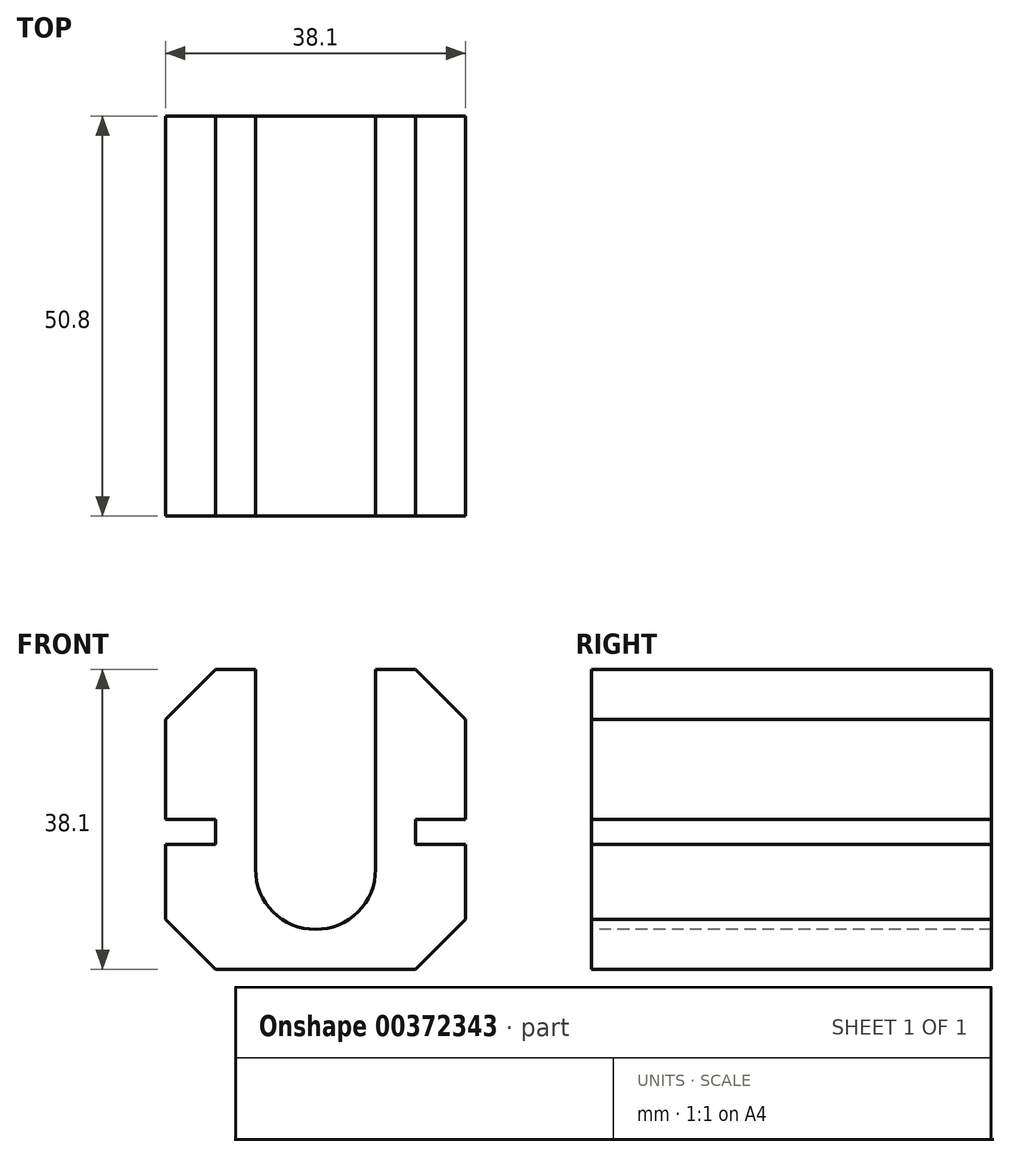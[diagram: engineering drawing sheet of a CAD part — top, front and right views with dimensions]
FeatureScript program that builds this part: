
annotation { "Feature Type Name" : "Feature", "Feature Type Description" : "" }
export const myFeature = defineFeature(function(context is Context, id is Id, definition is map)
    precondition{}
    {
        {
            var Q0;
            Q0=qCreatedBy(makeId("Front.planeOp"),FACE);
            var sketch = newSketch(context, id + "F0", { "sketchPlane" : qUnion([Q0])});
            skLineSegment(sketch, "E0", {"start": v(-12.7, 19.05) * mm, "end": v(-19.05, 12.7) * mm});
            skLineSegment(sketch, "E1", {"start": v(12.7, 19.05) * mm, "end": v(19.05, 12.7) * mm});
            skLineSegment(sketch, "E2", {"start": v(-12.7, -19.05) * mm, "end": v(-19.05, -12.7) * mm});
            skLineSegment(sketch, "E3", {"start": v(12.7, -19.05) * mm, "end": v(19.05, -12.7) * mm});
            skLineSegment(sketch, "E4", {"start": v(-12.7, 19.05) * mm, "end": v(12.7, 19.05) * mm});
            skLineSegment(sketch, "E5", {"start": v(-19.05, 12.7) * mm, "end": v(-19.05, -12.7) * mm});
            skLineSegment(sketch, "E6", {"start": v(19.05, 12.7) * mm, "end": v(19.05, -12.7) * mm});
            skLineSegment(sketch, "E7", {"start": v(-12.7, -19.05) * mm, "end": v(12.7, -19.05) * mm});
            skSolve(sketch);
        }
        {
            var Q0;
            Q0=qCreatedBy(makeId("Front.planeOp"),FACE);
            var sketch = newSketch(context, id + "F1", { "sketchPlane" : qUnion([Q0])});
            skLineSegment(sketch, "E8.bottom", {"start": v(-19.05, 0) * mm, "end": v(-12.7, 0) * mm});
            skLineSegment(sketch, "E8.top", {"start": v(-19.05, -3.18) * mm, "end": v(-12.7, -3.18) * mm});
            skLineSegment(sketch, "E8.left", {"start": v(-19.05, 0) * mm, "end": v(-19.05, -3.18) * mm});
            skLineSegment(sketch, "E8.right", {"start": v(-12.7, 0) * mm, "end": v(-12.7, -3.18) * mm});
            skSolve(sketch);
        }
        {
            var Q0;
            Q0=qCreatedBy(makeId("Front.planeOp"),FACE);
            var sketch = newSketch(context, id + "F2", { "sketchPlane" : qUnion([Q0])});
            skLineSegment(sketch, "E9.bottom", {"start": v(12.7, 0) * mm, "end": v(19.05, 0) * mm});
            skLineSegment(sketch, "E9.top", {"start": v(12.7, -3.17) * mm, "end": v(19.05, -3.17) * mm});
            skLineSegment(sketch, "E9.left", {"start": v(12.7, 0) * mm, "end": v(12.7, -3.17) * mm});
            skLineSegment(sketch, "E9.right", {"start": v(19.05, 0) * mm, "end": v(19.05, -3.17) * mm});
            skSolve(sketch);
        }
        {
            var Q0;
            Q0=qSketchRegion(id+"F0",true);
            extrude(context, id + "F3", {"entities" : qUnion([Q0]), "endBound" : BoundingType.SYMMETRIC, "depth" : 50.8 * mm});
        }
        {
            var Q0;
            Q0 = qSketchRegion(id + "F2", true);
            var Q1;
            Q1 = qSketchRegion(id + "F1", true);
            extrude(context, id + "F4", {"entities" : qUnion([Q0, Q1]), "operationType" : NewBodyOperationType.REMOVE, "endBound" : BoundingType.SYMMETRIC, "oppositeDirection" : true, "depth" : 50.8 * mm});
        }
        {
            var Q0;
            Q0=qCreatedBy(makeId("Front.planeOp"),FACE);
            var sketch = newSketch(context, id + "F5", { "sketchPlane" : qUnion([Q0])});
            skLineSegment(sketch, "E10.bottom", {"start": v(-7.62, 19.05) * mm, "end": v(7.62, 19.05) * mm});
            skLineSegment(sketch, "E10.left", {"start": v(-7.62, 19.05) * mm, "end": v(-7.62, -6.35) * mm});
            skLineSegment(sketch, "E10.right", {"start": v(7.62, 19.05) * mm, "end": v(7.62, -6.35) * mm});
            skArc(sketch, "E11", {"start": v(-7.62, -6.35) * mm, "mid": v(0, -13.97) * mm, "end": v(7.62, -6.35) * mm});
            skSolve(sketch);
        }
        {
            var Q0;
            Q0 = qSketchRegion(id + "F5", true);
            extrude(context, id + "F6", {"entities" : qUnion([Q0]), "operationType" : NewBodyOperationType.REMOVE, "endBound" : BoundingType.SYMMETRIC, "oppositeDirection" : true, "depth" : 50.8 * mm});
        }
    });
